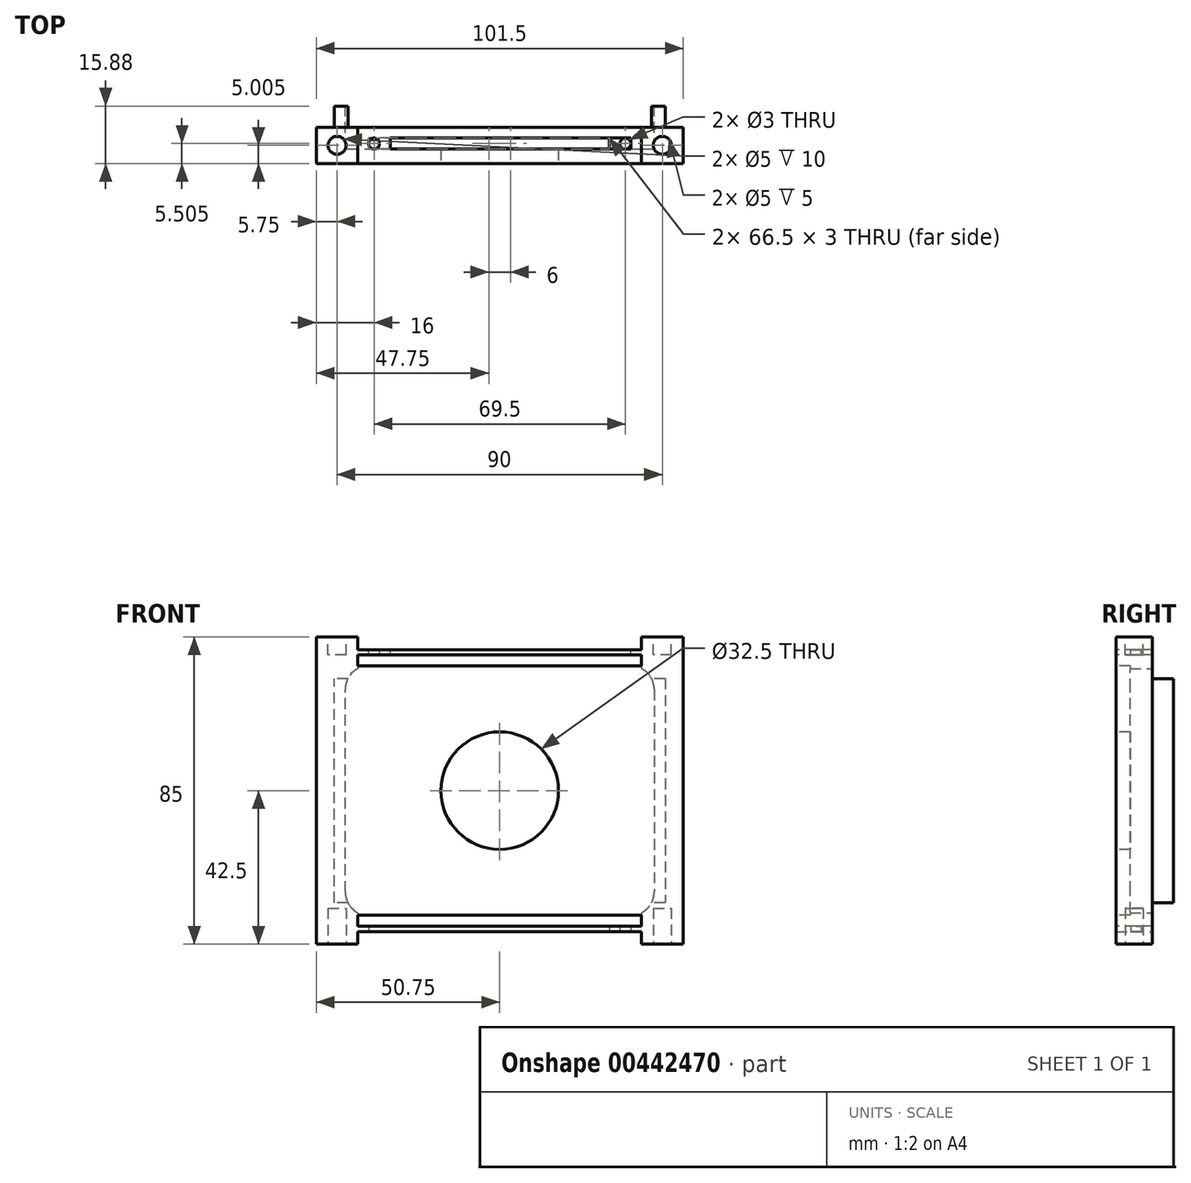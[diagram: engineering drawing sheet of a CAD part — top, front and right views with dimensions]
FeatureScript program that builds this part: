
annotation { "Feature Type Name" : "Feature", "Feature Type Description" : "" }
export const myFeature = defineFeature(function(context is Context, id is Id, definition is map)
    precondition{}
    {
        {
            var Q0;
            Q0=qCreatedBy(makeId("Front.planeOp"),FACE);
            var sketch = newSketch(context, id + "F0", { "sketchPlane" : qUnion([Q0])});
            skLineSegment(sketch, "E0.bottom", {"start": v(50.75, 42.5) * mm, "end": v(-50.75, 42.5) * mm});
            skLineSegment(sketch, "E0.top", {"start": v(50.75, -42.5) * mm, "end": v(-50.75, -42.5) * mm});
            skLineSegment(sketch, "E0.left", {"start": v(50.75, 42.5) * mm, "end": v(50.75, -42.5) * mm});
            skLineSegment(sketch, "E0.right", {"start": v(-50.75, 42.5) * mm, "end": v(-50.75, -42.5) * mm});
            skPoint(sketch, "E0.middle", {"position": v(0, 0) * mm});
            skSolve(sketch);
        }
        {
            var Q0;
            Q0=qSketchRegion(id+"F0",true);
            extrude(context, id + "F1", {"entities" : qUnion([Q0]), "depth" : 15.88 * mm});
        }
        {
            var Q0;
            Q0=makeQuery(id+"F1.opExtrude","CAP_FACE",FACE,{"disambiguationData":[OSD([sQuery(id+"F0.wireOp",EDGE,"E0.bottom"),sQuery(id+"F0.wireOp",EDGE,"E0.top"),sQuery(id+"F0.wireOp",EDGE,"E0.left"),sQuery(id+"F0.wireOp",EDGE,"E0.right")])],"isStart":false});
            var sketch = newSketch(context, id + "F2", { "sketchPlane" : qUnion([Q0])});
            skCircle(sketch, "E1", {"center": v(0, 0) * mm, "radius": 16.25 * mm});
            skSolve(sketch);
        }
        {
            var Q0;
            Q0=qSketchRegion(id+"F2",true);
            extrude(context, id + "F3", {"entities" : qUnion([Q0]), "operationType" : NewBodyOperationType.REMOVE, "oppositeDirection" : true, "depth" : 25 * mm});
        }
        {
            var Q0;
            Q0=makeQuery(id+"F1.opExtrude","CAP_FACE",FACE,{"disambiguationData":[OSD([sQuery(id+"F0.wireOp",EDGE,"E0.bottom"),sQuery(id+"F0.wireOp",EDGE,"E0.top"),sQuery(id+"F0.wireOp",EDGE,"E0.left"),sQuery(id+"F0.wireOp",EDGE,"E0.right")])],"isStart":true});
            var sketch = newSketch(context, id + "F4", { "sketchPlane" : qUnion([Q0])});
            skLineSegment(sketch, "E2.bottom", {"start": v(45.75, 37.5) * mm, "end": v(-45.75, 37.5) * mm, "construction": true});
            skLineSegment(sketch, "E2.top", {"start": v(45.75, -37.5) * mm, "end": v(-45.75, -37.5) * mm, "construction": true});
            skLineSegment(sketch, "E2.left", {"start": v(45.75, 37.5) * mm, "end": v(45.75, -37.5) * mm, "construction": true});
            skLineSegment(sketch, "E2.right", {"start": v(-45.75, 37.5) * mm, "end": v(-45.75, -37.5) * mm, "construction": true});
            skPoint(sketch, "E2.middle", {"position": v(0, 0) * mm});
            skCircle(sketch, "E3", {"center": v(-39.25, 31) * mm, "radius": 6.5 * mm, "construction": true});
            skCircle(sketch, "E4", {"center": v(-39.25, -31) * mm, "radius": 6.5 * mm, "construction": true});
            skCircle(sketch, "E5", {"center": v(39.25, -31) * mm, "radius": 6.5 * mm, "construction": true});
            skCircle(sketch, "E6", {"center": v(39.25, 31) * mm, "radius": 6.5 * mm, "construction": true});
            skLineSegment(sketch, "E7", {"start": v(-45.75, 31) * mm, "end": v(-45.75, -31) * mm});
            skLineSegment(sketch, "E8", {"start": v(-39.25, -37.5) * mm, "end": v(39.25, -37.5) * mm});
            skLineSegment(sketch, "E9", {"start": v(45.75, -31) * mm, "end": v(45.75, 31) * mm});
            skLineSegment(sketch, "E10", {"start": v(39.25, 37.5) * mm, "end": v(-39.25, 37.5) * mm});
            skArc(sketch, "E11", {"start": v(-39.25, 37.5) * mm, "mid": v(-43.85, 35.6) * mm, "end": v(-45.75, 31) * mm});
            skArc(sketch, "E12", {"start": v(-45.75, -31) * mm, "mid": v(-43.85, -35.6) * mm, "end": v(-39.25, -37.5) * mm});
            skArc(sketch, "E13", {"start": v(39.25, -37.5) * mm, "mid": v(43.85, -35.6) * mm, "end": v(45.75, -31) * mm});
            skArc(sketch, "E14", {"start": v(45.75, 31) * mm, "mid": v(43.85, 35.6) * mm, "end": v(39.25, 37.5) * mm});
            skLineSegment(sketch, "E15.bottom", {"start": v(50.75, 42.5) * mm, "end": v(-50.75, 42.5) * mm});
            skLineSegment(sketch, "E15.top", {"start": v(50.75, -42.5) * mm, "end": v(-50.75, -42.5) * mm});
            skLineSegment(sketch, "E15.left", {"start": v(50.75, 42.5) * mm, "end": v(50.75, -42.5) * mm});
            skLineSegment(sketch, "E15.right", {"start": v(-50.75, 42.5) * mm, "end": v(-50.75, -42.5) * mm});
            skSolve(sketch);
        }
        {
            var Q0;
            Q0=qSketchRegion(id+"F4",true);
            extrude(context, id + "F5", {"entities" : qUnion([Q0]), "operationType" : NewBodyOperationType.REMOVE, "oppositeDirection" : true, "depth" : 5.88 * mm});
        }
        {
            var Q0;
            Q0=makeQuery(id+"F1.opExtrude","CAP_FACE",FACE,{"disambiguationData":[OSD([sQuery(id+"F0.wireOp",EDGE,"E0.bottom"),sQuery(id+"F0.wireOp",EDGE,"E0.top"),sQuery(id+"F0.wireOp",EDGE,"E0.left"),sQuery(id+"F0.wireOp",EDGE,"E0.right")])],"isStart":true});
            var sketch = newSketch(context, id + "F6", { "sketchPlane" : qUnion([Q0])});
            skLineSegment(sketch, "E16.bottom", {"start": v(42.75, 34.5) * mm, "end": v(-42.75, 34.5) * mm, "construction": true});
            skLineSegment(sketch, "E16.top", {"start": v(42.75, -34.5) * mm, "end": v(-42.75, -34.5) * mm, "construction": true});
            skLineSegment(sketch, "E16.left", {"start": v(42.75, 34.5) * mm, "end": v(42.75, -34.5) * mm, "construction": true});
            skLineSegment(sketch, "E16.right", {"start": v(-42.75, 34.5) * mm, "end": v(-42.75, -34.5) * mm, "construction": true});
            skPoint(sketch, "E16.middle", {"position": v(0, 0) * mm});
            skCircle(sketch, "E17", {"center": v(-36.25, 28) * mm, "radius": 6.5 * mm, "construction": true});
            skCircle(sketch, "E18", {"center": v(-36.25, -28) * mm, "radius": 6.5 * mm, "construction": true});
            skCircle(sketch, "E19", {"center": v(36.25, -28) * mm, "radius": 6.5 * mm, "construction": true});
            skCircle(sketch, "E20", {"center": v(36.25, 28) * mm, "radius": 6.5 * mm, "construction": true});
            skLineSegment(sketch, "E21", {"start": v(-42.75, 28) * mm, "end": v(-42.75, -28) * mm});
            skLineSegment(sketch, "E22", {"start": v(-36.25, -34.5) * mm, "end": v(36.25, -34.5) * mm});
            skLineSegment(sketch, "E23", {"start": v(42.75, -28) * mm, "end": v(42.75, 28) * mm});
            skLineSegment(sketch, "E24", {"start": v(36.25, 34.5) * mm, "end": v(-36.25, 34.5) * mm});
            skArc(sketch, "E25", {"start": v(-36.25, 34.5) * mm, "mid": v(-40.85, 32.6) * mm, "end": v(-42.75, 28) * mm});
            skArc(sketch, "E26", {"start": v(-42.75, -28) * mm, "mid": v(-40.85, -32.6) * mm, "end": v(-36.25, -34.5) * mm});
            skArc(sketch, "E27", {"start": v(36.25, -34.5) * mm, "mid": v(40.85, -32.6) * mm, "end": v(42.75, -28) * mm});
            skArc(sketch, "E28", {"start": v(42.75, 28) * mm, "mid": v(40.85, 32.6) * mm, "end": v(36.25, 34.5) * mm});
            skSolve(sketch);
        }
        {
            var Q0;
            Q0=qSketchRegion(id+"F6",true);
            extrude(context, id + "F7", {"entities" : qUnion([Q0]), "operationType" : NewBodyOperationType.REMOVE, "oppositeDirection" : true, "depth" : 12 * mm});
        }
        {
            var Q0;
            Q0=makeQuery(id+"F1.opExtrude","SWEPT_FACE",FACE,{"disambiguationData":[OSD([sQuery(id+"F0.wireOp",EDGE,"E0.bottom")])]});
            var sketch = newSketch(context, id + "F8", { "sketchPlane" : qUnion([Q0])});
            skLineSegment(sketch, "E29.bottom", {"start": v(-39.25, -5.88) * mm, "end": v(39.25, -5.88) * mm});
            skLineSegment(sketch, "E29.top", {"start": v(-39.25, -15.88) * mm, "end": v(39.25, -15.88) * mm});
            skLineSegment(sketch, "E29.left", {"start": v(-39.25, -5.88) * mm, "end": v(-39.25, -15.88) * mm});
            skLineSegment(sketch, "E29.right", {"start": v(39.25, -5.88) * mm, "end": v(39.25, -15.88) * mm});
            skSolve(sketch);
        }
        {
            var Q0;
            Q0=qSketchRegion(id+"F8",true);
            extrude(context, id + "F9", {"entities" : qUnion([Q0]), "operationType" : NewBodyOperationType.REMOVE, "oppositeDirection" : true, "depth" : 3.5 * mm});
        }
        {
            var Q0;
            Q0=makeQuery(id+"F1.opExtrude","SWEPT_FACE",FACE,{"disambiguationData":[OSD([sQuery(id+"F0.wireOp",EDGE,"E0.top")])]});
            var sketch = newSketch(context, id + "F10", { "sketchPlane" : qUnion([Q0])});
            skLineSegment(sketch, "E30.bottom", {"start": v(-39.25, 15.88) * mm, "end": v(39.25, 15.88) * mm});
            skLineSegment(sketch, "E30.top", {"start": v(-39.25, 5.88) * mm, "end": v(39.25, 5.88) * mm});
            skLineSegment(sketch, "E30.left", {"start": v(-39.25, 15.88) * mm, "end": v(-39.25, 5.88) * mm});
            skLineSegment(sketch, "E30.right", {"start": v(39.25, 15.88) * mm, "end": v(39.25, 5.88) * mm});
            skSolve(sketch);
        }
        {
            var Q0;
            Q0=qSketchRegion(id+"F10",true);
            extrude(context, id + "F11", {"entities" : qUnion([Q0]), "operationType" : NewBodyOperationType.REMOVE, "oppositeDirection" : true, "depth" : 3.5 * mm});
        }
        {
            var Q0;
            Q0=makeQuery(id+"F1.opExtrude","CAP_FACE",FACE,{"disambiguationData":[OSD([sQuery(id+"F0.wireOp",EDGE,"E0.bottom"),sQuery(id+"F0.wireOp",EDGE,"E0.top"),sQuery(id+"F0.wireOp",EDGE,"E0.left"),sQuery(id+"F0.wireOp",EDGE,"E0.right")])],"isStart":false});
            var sketch = newSketch(context, id + "F12", { "sketchPlane" : qUnion([Q0])});
            skLineSegment(sketch, "E31.bottom", {"start": v(-39.25, 37.5) * mm, "end": v(39.25, 37.5) * mm});
            skLineSegment(sketch, "E31.top", {"start": v(-39.25, 34.5) * mm, "end": v(39.25, 34.5) * mm});
            skLineSegment(sketch, "E31.left", {"start": v(-39.25, 37.5) * mm, "end": v(-39.25, 34.5) * mm});
            skLineSegment(sketch, "E31.right", {"start": v(39.25, 37.5) * mm, "end": v(39.25, 34.5) * mm});
            skLineSegment(sketch, "E32.bottom", {"start": v(39.25, -37.5) * mm, "end": v(-39.25, -37.5) * mm});
            skLineSegment(sketch, "E32.top", {"start": v(39.25, -34.5) * mm, "end": v(-39.25, -34.5) * mm});
            skLineSegment(sketch, "E32.left", {"start": v(39.25, -37.5) * mm, "end": v(39.25, -34.5) * mm});
            skLineSegment(sketch, "E32.right", {"start": v(-39.25, -37.5) * mm, "end": v(-39.25, -34.5) * mm});
            skSolve(sketch);
        }
        {
            var Q0;
            Q0=qSketchRegion(id+"F12",true);
            extrude(context, id + "F13", {"entities" : qUnion([Q0]), "operationType" : NewBodyOperationType.REMOVE, "oppositeDirection" : true, "depth" : 25 * mm});
        }
        {
            var Q0;
            Q0=makeQuery(id+"F9.boolean.opBoolean","COPY",FACE,{"derivedFrom":makeQuery(id+"F9.opExtrude","CAP_FACE",FACE,{"disambiguationData":[OSD([sQuery(id+"F8.wireOp",EDGE,"E29.bottom"),sQuery(id+"F8.wireOp",EDGE,"E29.top"),sQuery(id+"F8.wireOp",EDGE,"E29.left"),sQuery(id+"F8.wireOp",EDGE,"E29.right")])],"isStart":false})});
            var sketch = newSketch(context, id + "F14", { "sketchPlane" : qUnion([Q0])});
            skLineSegment(sketch, "E33.bottom", {"start": v(-39.25, -5.88) * mm, "end": v(39.25, -5.88) * mm});
            skLineSegment(sketch, "E33.top", {"start": v(-39.25, 11.7) * mm, "end": v(39.25, 11.7) * mm});
            skLineSegment(sketch, "E33.left", {"start": v(-39.25, -5.88) * mm, "end": v(-39.25, 11.7) * mm});
            skLineSegment(sketch, "E33.right", {"start": v(39.25, -5.88) * mm, "end": v(39.25, 11.7) * mm});
            skSolve(sketch);
        }
        {
            var Q0;
            Q0=qSketchRegion(id+"F14",true);
            extrude(context, id + "F15", {"entities" : qUnion([Q0]), "operationType" : NewBodyOperationType.REMOVE, "oppositeDirection" : true, "depth" : 200 * mm});
        }
        {
            var Q0;
            Q0=makeQuery(id+"F5.boolean.opBoolean","COPY",FACE,{"derivedFrom":makeQuery(id+"F5.opExtrude","CAP_FACE",FACE,{"disambiguationData":[OSD([sQuery(id+"F4.wireOp",EDGE,"E7"),sQuery(id+"F4.wireOp",EDGE,"E8"),sQuery(id+"F4.wireOp",EDGE,"E9"),sQuery(id+"F4.wireOp",EDGE,"E10"),sQuery(id+"F4.wireOp",EDGE,"E11"),sQuery(id+"F4.wireOp",EDGE,"E12"),sQuery(id+"F4.wireOp",EDGE,"E13"),sQuery(id+"F4.wireOp",EDGE,"E14"),sQuery(id+"F4.wireOp",EDGE,"E15.bottom"),sQuery(id+"F4.wireOp",EDGE,"E15.top"),sQuery(id+"F4.wireOp",EDGE,"E15.left"),sQuery(id+"F4.wireOp",EDGE,"E15.right")])],"isStart":false})});
            var sketch = newSketch(context, id + "F16", { "sketchPlane" : qUnion([Q0])});
            skLineSegment(sketch, "E34.bottom", {"start": v(-39.25, 37.5) * mm, "end": v(39.25, 37.5) * mm});
            skLineSegment(sketch, "E34.top", {"start": v(-39.25, -37.5) * mm, "end": v(39.25, -37.5) * mm});
            skLineSegment(sketch, "E34.left", {"start": v(-39.25, 37.5) * mm, "end": v(-39.25, -37.5) * mm});
            skLineSegment(sketch, "E34.right", {"start": v(39.25, 37.5) * mm, "end": v(39.25, -37.5) * mm});
            skSolve(sketch);
        }
        {
            var Q0;
            Q0=qSketchRegion(id+"F16",true);
            extrude(context, id + "F17", {"entities" : qUnion([Q0]), "operationType" : NewBodyOperationType.REMOVE, "oppositeDirection" : true, "depth" : 6.12 * mm});
        }
        {
            var Q0;
            Q0=makeQuery(id+"F9.boolean.opBoolean","COPY",FACE,{"derivedFrom":makeQuery(id+"F9.opExtrude","CAP_FACE",FACE,{"disambiguationData":[OSD([sQuery(id+"F8.wireOp",EDGE,"E29.bottom"),sQuery(id+"F8.wireOp",EDGE,"E29.top"),sQuery(id+"F8.wireOp",EDGE,"E29.left"),sQuery(id+"F8.wireOp",EDGE,"E29.right")])],"isStart":false})});
            var sketch = newSketch(context, id + "F18", { "sketchPlane" : qUnion([Q0])});
            skCircle(sketch, "E35", {"center": v(-34.75, -10.38) * mm, "radius": 1.5 * mm});
            skLineSegment(sketch, "E36.bottom", {"start": v(-30.25, -8.88) * mm, "end": v(36.25, -8.87) * mm});
            skLineSegment(sketch, "E36.top", {"start": v(-30.25, -11.88) * mm, "end": v(36.25, -11.87) * mm});
            skLineSegment(sketch, "E36.left", {"start": v(-30.25, -8.88) * mm, "end": v(-30.25, -11.88) * mm});
            skLineSegment(sketch, "E36.right", {"start": v(36.25, -8.87) * mm, "end": v(36.25, -11.87) * mm});
            skSolve(sketch);
        }
        {
            var Q0;
            Q0=qSketchRegion(id+"F18",true);
            extrude(context, id + "F19", {"entities" : qUnion([Q0]), "operationType" : NewBodyOperationType.REMOVE, "oppositeDirection" : true, "depth" : 2 * mm});
        }
        {
            var Q0;
            Q0=makeQuery(id+"F11.boolean.opBoolean","COPY",FACE,{"derivedFrom":makeQuery(id+"F11.opExtrude","CAP_FACE",FACE,{"disambiguationData":[OSD([sQuery(id+"F10.wireOp",EDGE,"E30.bottom"),sQuery(id+"F10.wireOp",EDGE,"E30.top"),sQuery(id+"F10.wireOp",EDGE,"E30.left"),sQuery(id+"F10.wireOp",EDGE,"E30.right")])],"isStart":false})});
            var sketch = newSketch(context, id + "F20", { "sketchPlane" : qUnion([Q0])});
            skCircle(sketch, "E37", {"center": v(34.75, 10.38) * mm, "radius": 1.5 * mm});
            skLineSegment(sketch, "E38.bottom", {"start": v(-36.25, 11.87) * mm, "end": v(30.25, 11.88) * mm});
            skLineSegment(sketch, "E38.top", {"start": v(-36.25, 8.87) * mm, "end": v(30.25, 8.88) * mm});
            skLineSegment(sketch, "E38.left", {"start": v(-36.25, 11.88) * mm, "end": v(-36.25, 8.87) * mm});
            skLineSegment(sketch, "E38.right", {"start": v(30.25, 11.88) * mm, "end": v(30.25, 8.88) * mm});
            skSolve(sketch);
        }
        {
            var Q0;
            Q0=qSketchRegion(id+"F20",true);
            extrude(context, id + "F21", {"entities" : qUnion([Q0]), "operationType" : NewBodyOperationType.REMOVE, "oppositeDirection" : true, "depth" : 2 * mm});
        }
        {
            var Q0;
            {var subQ0=sQuery(id+"F0.wireOp",EDGE,"E0.right");var subQ1=sQuery(id+"F0.wireOp",EDGE,"E0.top");Q0=makeQuery(id+"F11.boolean.opBoolean","SPLIT",FACE,{"disambiguationData":[TD([makeQuery(id+"F1.opExtrude","SWEPT_FACE",FACE,{"disambiguationData":[OSD([subQ0])]})])],"derivedFrom":makeQuery(id+"F1.opExtrude","SWEPT_FACE",FACE,{"disambiguationData":[OSD([subQ1])]})});}
            var sketch = newSketch(context, id + "F22", { "sketchPlane" : qUnion([Q0])});
            skLineSegment(sketch, "E39", {"start": v(-50.75, 15.87) * mm, "end": v(-39.25, 5.87) * mm, "construction": true});
            skLineSegment(sketch, "E40", {"start": v(-39.25, 5.88) * mm, "end": v(50.77, 5.88) * mm, "construction": true});
            skLineSegment(sketch, "E41", {"start": v(50.77, 5.87) * mm, "end": v(66.59, 13.67) * mm, "construction": true});
            skLineSegment(sketch, "E42", {"start": v(66.59, 13.67) * mm, "end": v(61.79, 23.42) * mm, "construction": true});
            skLineSegment(sketch, "E43", {"start": v(-39.25, 15.88) * mm, "end": v(-50.75, 5.88) * mm, "construction": true});
            skCircle(sketch, "E44", {"center": v(-45, 10.87) * mm, "radius": 2.5 * mm});
            skSolve(sketch);
        }
        {
            var Q0;
            Q0=qSketchRegion(id+"F22",true);
            extrude(context, id + "F23", {"entities" : qUnion([Q0]), "operationType" : NewBodyOperationType.REMOVE, "oppositeDirection" : true, "depth" : 10 * mm});
        }
        {
            var Q0;
            {var subQ0=sQuery(id+"F0.wireOp",EDGE,"E0.left");var subQ1=sQuery(id+"F0.wireOp",EDGE,"E0.top");Q0=makeQuery(id+"F11.boolean.opBoolean","SPLIT",FACE,{"disambiguationData":[TD([makeQuery(id+"F1.opExtrude","SWEPT_FACE",FACE,{"disambiguationData":[OSD([subQ0])]})])],"derivedFrom":makeQuery(id+"F1.opExtrude","SWEPT_FACE",FACE,{"disambiguationData":[OSD([subQ1])]})});}
            var sketch = newSketch(context, id + "F24", { "sketchPlane" : qUnion([Q0])});
            skLineSegment(sketch, "E45", {"start": v(39.25, 15.88) * mm, "end": v(50.75, 5.88) * mm, "construction": true});
            skLineSegment(sketch, "E46", {"start": v(50.75, 5.88) * mm, "end": v(50.75, 15.88) * mm, "construction": true});
            skLineSegment(sketch, "E47", {"start": v(50.75, 15.88) * mm, "end": v(39.25, 5.88) * mm, "construction": true});
            skCircle(sketch, "E48", {"center": v(45, 10.88) * mm, "radius": 2.5 * mm});
            skSolve(sketch);
        }
        {
            var Q0;
            Q0=qSketchRegion(id+"F24",true);
            extrude(context, id + "F25", {"entities" : qUnion([Q0]), "operationType" : NewBodyOperationType.REMOVE, "oppositeDirection" : true, "depth" : 10 * mm});
        }
        {
            var Q0;
            {var subQ0=sQuery(id+"F0.wireOp",EDGE,"E0.right");var subQ1=sQuery(id+"F0.wireOp",EDGE,"E0.bottom");Q0=makeQuery(id+"F9.boolean.opBoolean","SPLIT",FACE,{"disambiguationData":[TD([makeQuery(id+"F1.opExtrude","SWEPT_FACE",FACE,{"disambiguationData":[OSD([subQ0])]})])],"derivedFrom":makeQuery(id+"F1.opExtrude","SWEPT_FACE",FACE,{"disambiguationData":[OSD([subQ1])]})});}
            var sketch = newSketch(context, id + "F26", { "sketchPlane" : qUnion([Q0])});
            skLineSegment(sketch, "E49", {"start": v(-50.75, -5.88) * mm, "end": v(-39.25, -15.88) * mm, "construction": true});
            skLineSegment(sketch, "E50", {"start": v(-39.25, -15.88) * mm, "end": v(-39.25, -5.88) * mm, "construction": true});
            skLineSegment(sketch, "E51", {"start": v(-39.25, -5.88) * mm, "end": v(-50.75, -15.88) * mm, "construction": true});
            skCircle(sketch, "E52", {"center": v(-45, -10.88) * mm, "radius": 2.5 * mm});
            skSolve(sketch);
        }
        {
            var Q0;
            Q0=qSketchRegion(id+"F26",true);
            extrude(context, id + "F27", {"entities" : qUnion([Q0]), "operationType" : NewBodyOperationType.REMOVE, "oppositeDirection" : true, "depth" : 5 * mm});
        }
        {
            var Q0;
            {var subQ0=sQuery(id+"F0.wireOp",EDGE,"E0.left");var subQ1=sQuery(id+"F0.wireOp",EDGE,"E0.bottom");Q0=makeQuery(id+"F9.boolean.opBoolean","SPLIT",FACE,{"disambiguationData":[TD([makeQuery(id+"F1.opExtrude","SWEPT_FACE",FACE,{"disambiguationData":[OSD([subQ0])]})])],"derivedFrom":makeQuery(id+"F1.opExtrude","SWEPT_FACE",FACE,{"disambiguationData":[OSD([subQ1])]})});}
            var sketch = newSketch(context, id + "F28", { "sketchPlane" : qUnion([Q0])});
            skLineSegment(sketch, "E53", {"start": v(50.75, -5.87) * mm, "end": v(39.25, -15.87) * mm, "construction": true});
            skLineSegment(sketch, "E54", {"start": v(39.25, -15.87) * mm, "end": v(39.25, -5.88) * mm, "construction": true});
            skLineSegment(sketch, "E55", {"start": v(39.25, -5.88) * mm, "end": v(50.75, -15.88) * mm, "construction": true});
            skCircle(sketch, "E56", {"center": v(45, -10.88) * mm, "radius": 2.5 * mm});
            skSolve(sketch);
        }
        {
            var Q0;
            Q0=qSketchRegion(id+"F28",true);
            extrude(context, id + "F29", {"entities" : qUnion([Q0]), "operationType" : NewBodyOperationType.REMOVE, "oppositeDirection" : true, "depth" : 5 * mm});
        }
        {
            var Q0;
            Q0=makeQuery(id+"F13.boolean.opBoolean","SPLIT",FACE,{"disambiguationData":[TD([makeQuery(id+"F5.boolean.opBoolean","COPY",FACE,{"derivedFrom":makeQuery(id+"F5.opExtrude","SWEPT_FACE",FACE,{"disambiguationData":[OSD([sQuery(id+"F4.wireOp",EDGE,"E7")])]})})])],"derivedFrom":makeQuery(id+"F1.opExtrude","CAP_FACE",FACE,{"disambiguationData":[OSD([sQuery(id+"F0.wireOp",EDGE,"E0.bottom"),sQuery(id+"F0.wireOp",EDGE,"E0.top"),sQuery(id+"F0.wireOp",EDGE,"E0.left"),sQuery(id+"F0.wireOp",EDGE,"E0.right")])],"isStart":true})});
            var sketch = newSketch(context, id + "F30", { "sketchPlane" : qUnion([Q0])});
            skLineSegment(sketch, "E57.bottom", {"start": v(-45.75, 31) * mm, "end": v(45.83, 31) * mm});
            skLineSegment(sketch, "E57.top", {"start": v(-45.75, 37.95) * mm, "end": v(45.83, 37.95) * mm});
            skLineSegment(sketch, "E57.left", {"start": v(-45.75, 31) * mm, "end": v(-45.75, 37.95) * mm});
            skLineSegment(sketch, "E57.right", {"start": v(45.83, 31) * mm, "end": v(45.83, 37.95) * mm});
            skLineSegment(sketch, "E58.bottom", {"start": v(-45.75, -31) * mm, "end": v(47.3, -31) * mm});
            skLineSegment(sketch, "E58.top", {"start": v(-45.75, -40.17) * mm, "end": v(47.3, -40.17) * mm});
            skLineSegment(sketch, "E58.left", {"start": v(-45.75, -31) * mm, "end": v(-45.75, -40.17) * mm});
            skLineSegment(sketch, "E58.right", {"start": v(47.3, -31) * mm, "end": v(47.3, -40.17) * mm});
            skSolve(sketch);
        }
        {
            var Q0;
            Q0 = qSketchRegion(id + "F30", true);
            extrude(context, id + "F31", {"entities" : qUnion([Q0]), "operationType" : NewBodyOperationType.REMOVE, "oppositeDirection" : true, "depth" : 5.88 * mm});
        }
    });
